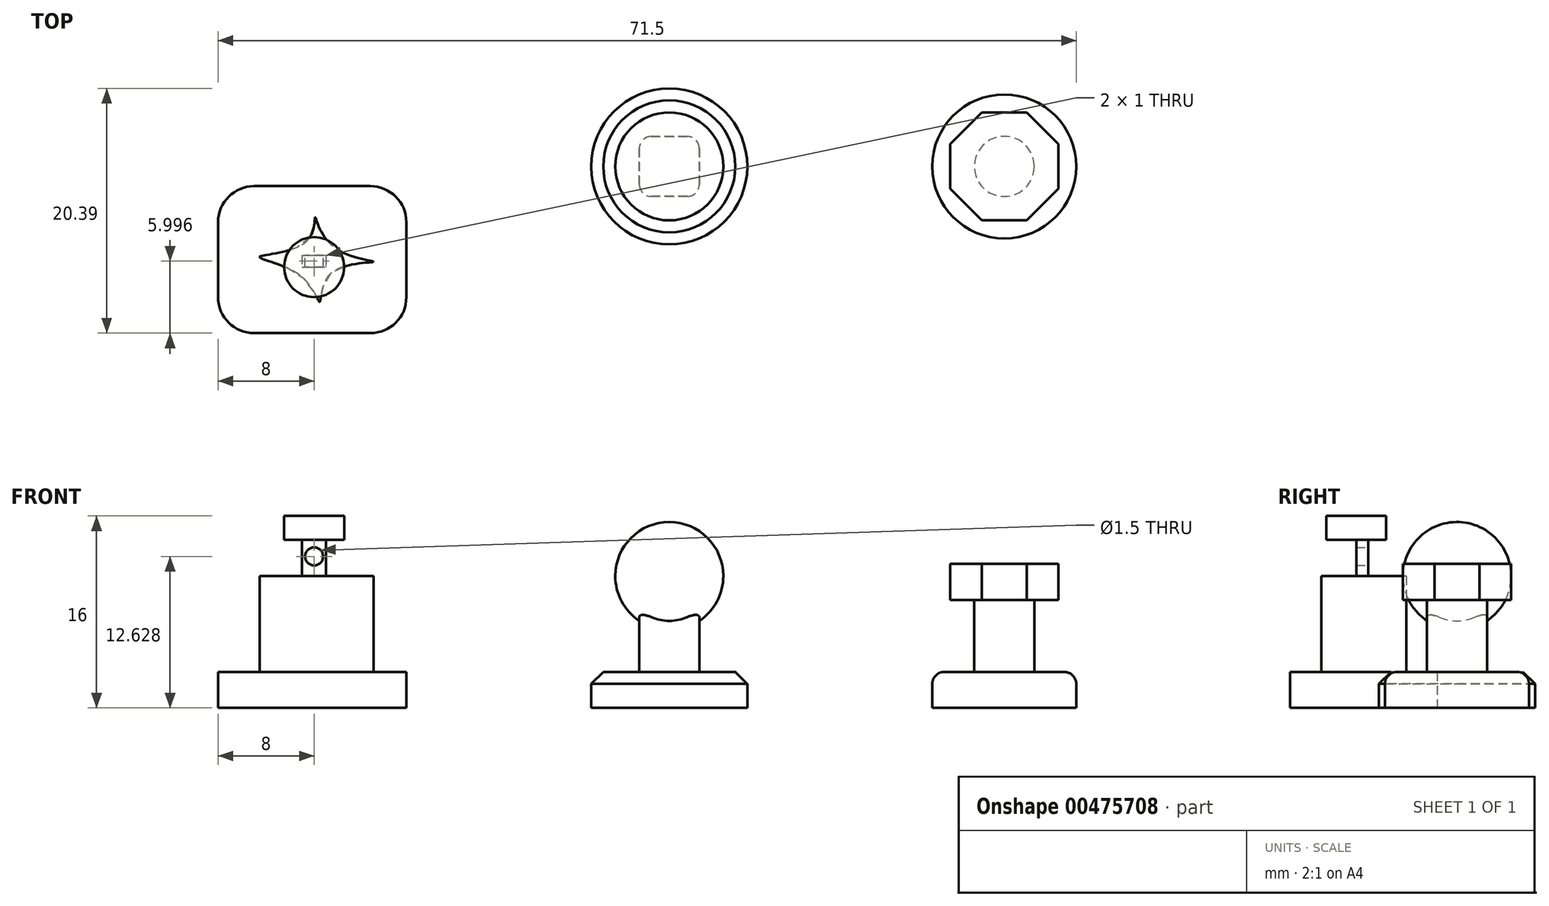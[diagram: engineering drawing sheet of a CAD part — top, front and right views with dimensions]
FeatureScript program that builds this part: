
annotation { "Feature Type Name" : "Feature", "Feature Type Description" : "" }
export const myFeature = defineFeature(function(context is Context, id is Id, definition is map)
    precondition{}
    {
        {
            var Q0;
            Q0=qCreatedBy(makeId("Top.planeOp"),FACE);
            var sketch = newSketch(context, id + "F0", { "sketchPlane" : qUnion([Q0])});
            skCircle(sketch, "E0", {"center": v(0, 0) * mm, "radius": 6.5 * mm});
            skSolve(sketch);
        }
        {
            var Q0;
            Q0=makeQuery(id+"F0.imprint","IMPRINT",FACE,{"disambiguationData":[TD([[makeQuery(id+"F0.imprint","IMPRINT",EDGE,{"derivedFrom":sQuery(id+"F0.wireOp",EDGE,"E0")}),1.0]])]});
            extrude(context, id + "F1", {"entities" : qUnion([Q0]), "depth" : 3 * mm});
        }
        {
            var Q0;
            Q0=makeQuery(id+"F1.opExtrude","CAP_FACE",FACE,{"disambiguationData":[OSD([sQuery(id+"F0.wireOp",EDGE,"E0")])],"isStart":false});
            var sketch = newSketch(context, id + "F2", { "sketchPlane" : qUnion([Q0])});
            skLineSegment(sketch, "E1.bottom", {"start": v(2.5, 2.5) * mm, "end": v(-2.5, 2.5) * mm});
            skLineSegment(sketch, "E1.top", {"start": v(2.5, -2.5) * mm, "end": v(-2.5, -2.5) * mm});
            skLineSegment(sketch, "E1.left", {"start": v(2.5, 2.5) * mm, "end": v(2.5, -2.5) * mm});
            skLineSegment(sketch, "E1.right", {"start": v(-2.5, 2.5) * mm, "end": v(-2.5, -2.5) * mm});
            skPoint(sketch, "E1.middle", {"position": v(0, 0) * mm});
            skSolve(sketch);
        }
        {
            var Q0;
            Q0 = qSketchRegion(id + "F2", true);
            extrude(context, id + "F3", {"entities" : qUnion([Q0]), "operationType" : NewBodyOperationType.ADD, "depth" : 8 * mm});
        }
        {
            var Q0;
            Q0=makeQuery(id+"F3.opExtrude","CAP_FACE",FACE,{"disambiguationData":[OSD([sQuery(id+"F2.wireOp",EDGE,"E1.bottom"),sQuery(id+"F2.wireOp",EDGE,"E1.top"),sQuery(id+"F2.wireOp",EDGE,"E1.left"),sQuery(id+"F2.wireOp",EDGE,"E1.right")])],"isStart":false});
            var sketch = newSketch(context, id + "F4", { "sketchPlane" : qUnion([Q0])});
            skArc(sketch, "E2", {"start": v(-4.5, 0) * mm, "mid": v(0, -4.5) * mm, "end": v(4.5, 0) * mm});
            skLineSegment(sketch, "E3", {"start": v(-4.5, 0) * mm, "end": v(4.5, 0) * mm});
            skSolve(sketch);
        }
        {
            var Q0;
            {var subQ1=sQuery(id+"F4.wireOp",EDGE,"E2");Q0=makeQuery(id+"F4.imprint","IMPRINT",FACE,{"disambiguationData":[TD([[makeQuery(id+"F4.imprint","IMPRINT",EDGE,{"derivedFrom":subQ1}),1.0]])]});}
            var Q1;
            {var subQ5=makeQuery(id+"F3.opExtrude","CAP_EDGE",EDGE,{"disambiguationData":[OSD([sQuery(id+"F2.wireOp",EDGE,"E1.top")])],"isStart":false});Q1=makeQuery(id+"F4.imprint","IMPRINT",FACE,{"disambiguationData":[TD([[makeQuery(id+"F4.imprint","IMPRINT",EDGE,{"derivedFrom":subQ5}),-1.0]])]});}
            var Q2;
            Q2=sQuery(id+"F4.wireOp",EDGE,"E3");
            revolve(context, id + "F5", {"operationType" : NewBodyOperationType.ADD, "entities" : qUnion([Q0, Q1]), "axis" : qUnion([Q2]), "revolveType" : RevolveType.FULL});
        }
        {
            var Q0;
            Q0=qCreatedBy(makeId("Top.planeOp"),FACE);
            var sketch = newSketch(context, id + "F6", { "sketchPlane" : qUnion([Q0])});
            skCircle(sketch, "E4", {"center": v(27.91, 0) * mm, "radius": 6 * mm});
            skSolve(sketch);
        }
        {
            var Q0;
            Q0 = qSketchRegion(id + "F6", true);
            extrude(context, id + "F7", {"entities" : qUnion([Q0]), "depth" : 3 * mm});
        }
        {
            var Q0;
            Q0=makeQuery(id+"F7.opExtrude","CAP_FACE",FACE,{"disambiguationData":[OSD([sQuery(id+"F6.wireOp",EDGE,"E4")])],"isStart":false});
            var sketch = newSketch(context, id + "F8", { "sketchPlane" : qUnion([Q0])});
            skCircle(sketch, "E5", {"center": v(27.91, 0) * mm, "radius": 2.5 * mm});
            skSolve(sketch);
        }
        {
            var Q0;
            Q0 = qSketchRegion(id + "F8", true);
            extrude(context, id + "F9", {"entities" : qUnion([Q0]), "operationType" : NewBodyOperationType.ADD, "depth" : 6 * mm});
        }
        {
            var Q0;
            Q0=makeQuery(id+"F9.opExtrude","CAP_FACE",FACE,{"disambiguationData":[OSD([sQuery(id+"F8.wireOp",EDGE,"E5")])],"isStart":false});
            var sketch = newSketch(context, id + "F10", { "sketchPlane" : qUnion([Q0])});
            skCircle(sketch, "E6.cCircle", {"center": v(27.91, 0) * mm, "radius": 4.5 * mm, "construction": true});
            skLineSegment(sketch, "E6.0", {"start": v(26.05, 4.5) * mm, "end": v(29.78, 4.5) * mm});
            skLineSegment(sketch, "E6.1", {"start": v(29.78, 4.5) * mm, "end": v(32.41, 1.86) * mm});
            skLineSegment(sketch, "E6.2", {"start": v(32.41, 1.86) * mm, "end": v(32.41, -1.86) * mm});
            skLineSegment(sketch, "E6.3", {"start": v(32.41, -1.86) * mm, "end": v(29.78, -4.5) * mm});
            skLineSegment(sketch, "E6.4", {"start": v(29.78, -4.5) * mm, "end": v(26.05, -4.5) * mm});
            skLineSegment(sketch, "E6.5", {"start": v(26.05, -4.5) * mm, "end": v(23.41, -1.86) * mm});
            skLineSegment(sketch, "E6.6", {"start": v(23.41, -1.86) * mm, "end": v(23.41, 1.86) * mm});
            skLineSegment(sketch, "E6.7", {"start": v(23.41, 1.86) * mm, "end": v(26.05, 4.5) * mm});
            skPoint(sketch, "E6.0.midPoint", {"position": v(27.91, 4.5) * mm});
            skSolve(sketch);
        }
        {
            var Q0;
            Q0 = qSketchRegion(id + "F10", true);
            extrude(context, id + "F11", {"entities" : qUnion([Q0]), "operationType" : NewBodyOperationType.ADD, "depth" : 3 * mm});
        }
        {
            var Q0;
            Q0=makeQuery(id+"F7.opExtrude","CAP_EDGE",EDGE,{"disambiguationData":[OSD([sQuery(id+"F6.wireOp",EDGE,"E4")])],"isStart":false});
            var Q1;
            Q1=makeQuery(id+"F9.opExtrude","CAP_EDGE",EDGE,{"disambiguationData":[OSD([sQuery(id+"F8.wireOp",EDGE,"E5")])],"isStart":true});
            fillet(context, id + "F12", {"entities" : qUnion([Q0, Q1]), "radius" : 1 * mm, "tangentPropagation" : true, "allowEdgeOverflow" : false});
        }
        {
            var Q0;
            Q0=qCreatedBy(makeId("Top.planeOp"),FACE);
            var sketch = newSketch(context, id + "F13", { "sketchPlane" : qUnion([Q0])});
            skLineSegment(sketch, "E7.bottom", {"start": v(-21.9, -13.9) * mm, "end": v(-37.59, -13.9) * mm});
            skLineSegment(sketch, "E7.top", {"start": v(-21.9, -1.64) * mm, "end": v(-37.59, -1.64) * mm});
            skLineSegment(sketch, "E7.left", {"start": v(-21.9, -13.9) * mm, "end": v(-21.9, -1.64) * mm});
            skLineSegment(sketch, "E7.right", {"start": v(-37.59, -13.9) * mm, "end": v(-37.59, -1.64) * mm});
            skPoint(sketch, "E7.middle", {"position": v(-29.75, -7.77) * mm});
            skSolve(sketch);
        }
        {
            var Q0;
            Q0 = qSketchRegion(id + "F13", true);
            extrude(context, id + "F14", {"entities" : qUnion([Q0]), "depth" : 3 * mm});
        }
        {
            var Q0;
            Q0=makeQuery(id+"F14.opExtrude","CAP_FACE",FACE,{"disambiguationData":[OSD([sQuery(id+"F13.wireOp",EDGE,"E7.bottom"),sQuery(id+"F13.wireOp",EDGE,"E7.top"),sQuery(id+"F13.wireOp",EDGE,"E7.left"),sQuery(id+"F13.wireOp",EDGE,"E7.right")])],"isStart":false});
            var sketch = newSketch(context, id + "F15", { "sketchPlane" : qUnion([Q0])});
            skFitSpline(sketch, "E8", {"points": [v(-28.23, -8.94) * mm, v(-29.12, -11.29) * mm, v(-30.59, -9.22) * mm, v(-34.11, -7.54) * mm, v(-30.21, -6.24) * mm, v(-29.51, -4.24) * mm, v(-28.07, -6.63) * mm, v(-24.65, -7.96) * mm, v(-28.23, -8.94) * mm]});
            skSolve(sketch);
        }
        {
            var Q0;
            Q0 = qSketchRegion(id + "F15", true);
            extrude(context, id + "F16", {"entities" : qUnion([Q0]), "operationType" : NewBodyOperationType.ADD, "depth" : 8 * mm});
        }
        {
            var Q0;
            Q0=makeQuery(id+"F16.opExtrude","CAP_FACE",FACE,{"disambiguationData":[OSD([sQuery(id+"F15.wireOp",EDGE,"E8")])],"isStart":false});
            var sketch = newSketch(context, id + "F17", { "sketchPlane" : qUnion([Q0])});
            skLineSegment(sketch, "E9.bottom", {"start": v(-30.59, -7.4) * mm, "end": v(-28.59, -7.4) * mm});
            skLineSegment(sketch, "E9.top", {"start": v(-30.59, -8.4) * mm, "end": v(-28.59, -8.4) * mm});
            skLineSegment(sketch, "E9.left", {"start": v(-30.59, -7.4) * mm, "end": v(-30.59, -8.4) * mm});
            skLineSegment(sketch, "E9.right", {"start": v(-28.59, -7.4) * mm, "end": v(-28.59, -8.4) * mm});
            skPoint(sketch, "E9.middle", {"position": v(-29.59, -7.9) * mm});
            skSolve(sketch);
        }
        {
            var Q0;
            Q0 = qSketchRegion(id + "F17", true);
            extrude(context, id + "F18", {"entities" : qUnion([Q0]), "operationType" : NewBodyOperationType.ADD, "depth" : 3 * mm});
        }
        {
            var Q0;
            Q0=makeQuery(id+"F18.opExtrude","SWEPT_FACE",FACE,{"disambiguationData":[OSD([sQuery(id+"F17.wireOp",EDGE,"E9.bottom")])]});
            var sketch = newSketch(context, id + "F19", { "sketchPlane" : qUnion([Q0])});
            skCircle(sketch, "E10", {"center": v(29.59, 12.63) * mm, "radius": 0.75 * mm});
            skPoint(sketch, "E10.centerSnap0", {"position": v(29.59, 11) * mm});
            skSolve(sketch);
        }
        {
            var Q0;
            Q0 = qSketchRegion(id + "F19", true);
            extrude(context, id + "F20", {"entities" : qUnion([Q0]), "operationType" : NewBodyOperationType.REMOVE, "oppositeDirection" : true, "depth" : 25 * mm});
        }
        {
            var Q0;
            Q0=makeQuery(id+"F1.opExtrude","CAP_EDGE",EDGE,{"disambiguationData":[OSD([sQuery(id+"F0.wireOp",EDGE,"E0")])],"isStart":false});
            chamfer(context, id + "F21", {"entities" : qUnion([Q0]), "width" : 1 * mm, "tangentPropagation" : true});
        }
        {
            var Q0;
            Q0=makeQuery(id+"F3.opExtrude","SWEPT_EDGE",EDGE,{"disambiguationData":[OSD([sQuery(id+"F2.wireOp",EDGE,"E1.top"),sQuery(id+"F2.wireOp",EDGE,"E1.right")])]});
            var Q1;
            Q1=makeQuery(id+"F3.opExtrude","SWEPT_EDGE",EDGE,{"disambiguationData":[OSD([sQuery(id+"F2.wireOp",EDGE,"E1.bottom"),sQuery(id+"F2.wireOp",EDGE,"E1.right")])]});
            var Q2;
            Q2=makeQuery(id+"F3.opExtrude","SWEPT_EDGE",EDGE,{"disambiguationData":[OSD([sQuery(id+"F2.wireOp",EDGE,"E1.top"),sQuery(id+"F2.wireOp",EDGE,"E1.left")])]});
            var Q3;
            Q3=makeQuery(id+"F3.opExtrude","SWEPT_EDGE",EDGE,{"disambiguationData":[OSD([sQuery(id+"F2.wireOp",EDGE,"E1.bottom"),sQuery(id+"F2.wireOp",EDGE,"E1.left")])]});
            fillet(context, id + "F22", {"entities" : qUnion([Q0, Q1, Q2, Q3]), "radius" : 1 * mm, "tangentPropagation" : true, "allowEdgeOverflow" : false});
        }
        {
            var Q0;
            Q0=makeQuery(id+"F14.opExtrude","SWEPT_EDGE",EDGE,{"disambiguationData":[OSD([sQuery(id+"F13.wireOp",EDGE,"E7.bottom"),sQuery(id+"F13.wireOp",EDGE,"E7.right")])]});
            var Q1;
            Q1=makeQuery(id+"F14.opExtrude","SWEPT_EDGE",EDGE,{"disambiguationData":[OSD([sQuery(id+"F13.wireOp",EDGE,"E7.bottom"),sQuery(id+"F13.wireOp",EDGE,"E7.left")])]});
            var Q2;
            Q2=makeQuery(id+"F14.opExtrude","SWEPT_EDGE",EDGE,{"disambiguationData":[OSD([sQuery(id+"F13.wireOp",EDGE,"E7.top"),sQuery(id+"F13.wireOp",EDGE,"E7.left")])]});
            var Q3;
            Q3=makeQuery(id+"F14.opExtrude","SWEPT_EDGE",EDGE,{"disambiguationData":[OSD([sQuery(id+"F13.wireOp",EDGE,"E7.top"),sQuery(id+"F13.wireOp",EDGE,"E7.right")])]});
            fillet(context, id + "F23", {"entities" : qUnion([Q0, Q1, Q2, Q3]), "radius" : 3 * mm, "tangentPropagation" : true, "allowEdgeOverflow" : false});
        }
        {
            var Q0;
            Q0=makeQuery(id+"F18.opExtrude","CAP_FACE",FACE,{"disambiguationData":[OSD([sQuery(id+"F17.wireOp",EDGE,"E9.bottom"),sQuery(id+"F17.wireOp",EDGE,"E9.top"),sQuery(id+"F17.wireOp",EDGE,"E9.left"),sQuery(id+"F17.wireOp",EDGE,"E9.right")])],"isStart":false});
            var sketch = newSketch(context, id + "F24", { "sketchPlane" : qUnion([Q0])});
            skCircle(sketch, "E11", {"center": v(-29.59, -8.4) * mm, "radius": 2.5 * mm});
            skSolve(sketch);
        }
        {
            var Q0;
            Q0 = qSketchRegion(id + "F24", true);
            extrude(context, id + "F25", {"entities" : qUnion([Q0]), "operationType" : NewBodyOperationType.ADD, "depth" : 2 * mm});
        }
    });
